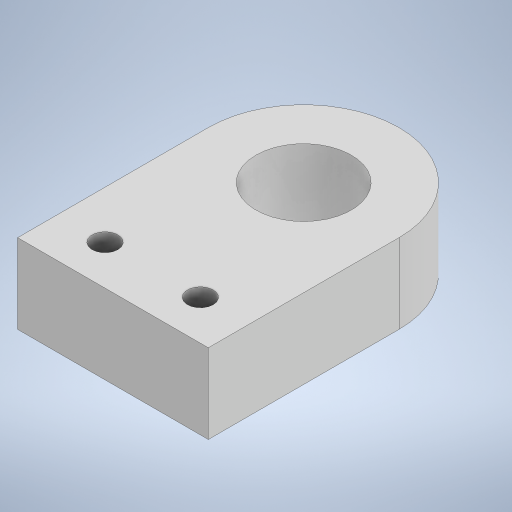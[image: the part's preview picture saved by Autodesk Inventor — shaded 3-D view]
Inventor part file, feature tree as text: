
AUTODESK INVENTOR PART (.ipt)
format: ipt  version: 2023.2 (Build 272271030, 271C)  size: 231,936 bytes
history: native  units: mm
features: extrude x3, sketch x3, projected_geometry x2
ambient origin geometry x8: Origin, YZ Plane, XZ Plane, XY Plane, X Axis, Y Axis, Z Axis, Center Point
bodies: Solid1 (feature_tree)
feature tree (8):
  extrude  "Extrusion1"  Depth=60.0mm
  extrude  "Extrusion2"  Depth=25.0mm TaperAngle=0.0deg
  extrude  "Extrusion3"  Depth=30.0mm
  sketch  "Sketch1"  dims[d0=60.0mm d1=60.0mm]
  sketch  "Sketch2"  dims[d2=30.0mm d3=25.0mm d4=0.0mm]
  projected_geometry  "Projected Loop1"
  sketch  "Sketch3"  dims[d5=65.0mm d6=8.1mm d7=30.0mm d8=0.0mm d9=0.0mm d10=8.1mm d11=8.1mm d12=3.0mm d13=0.0mm]
  projected_geometry  "Projected Loop2"
